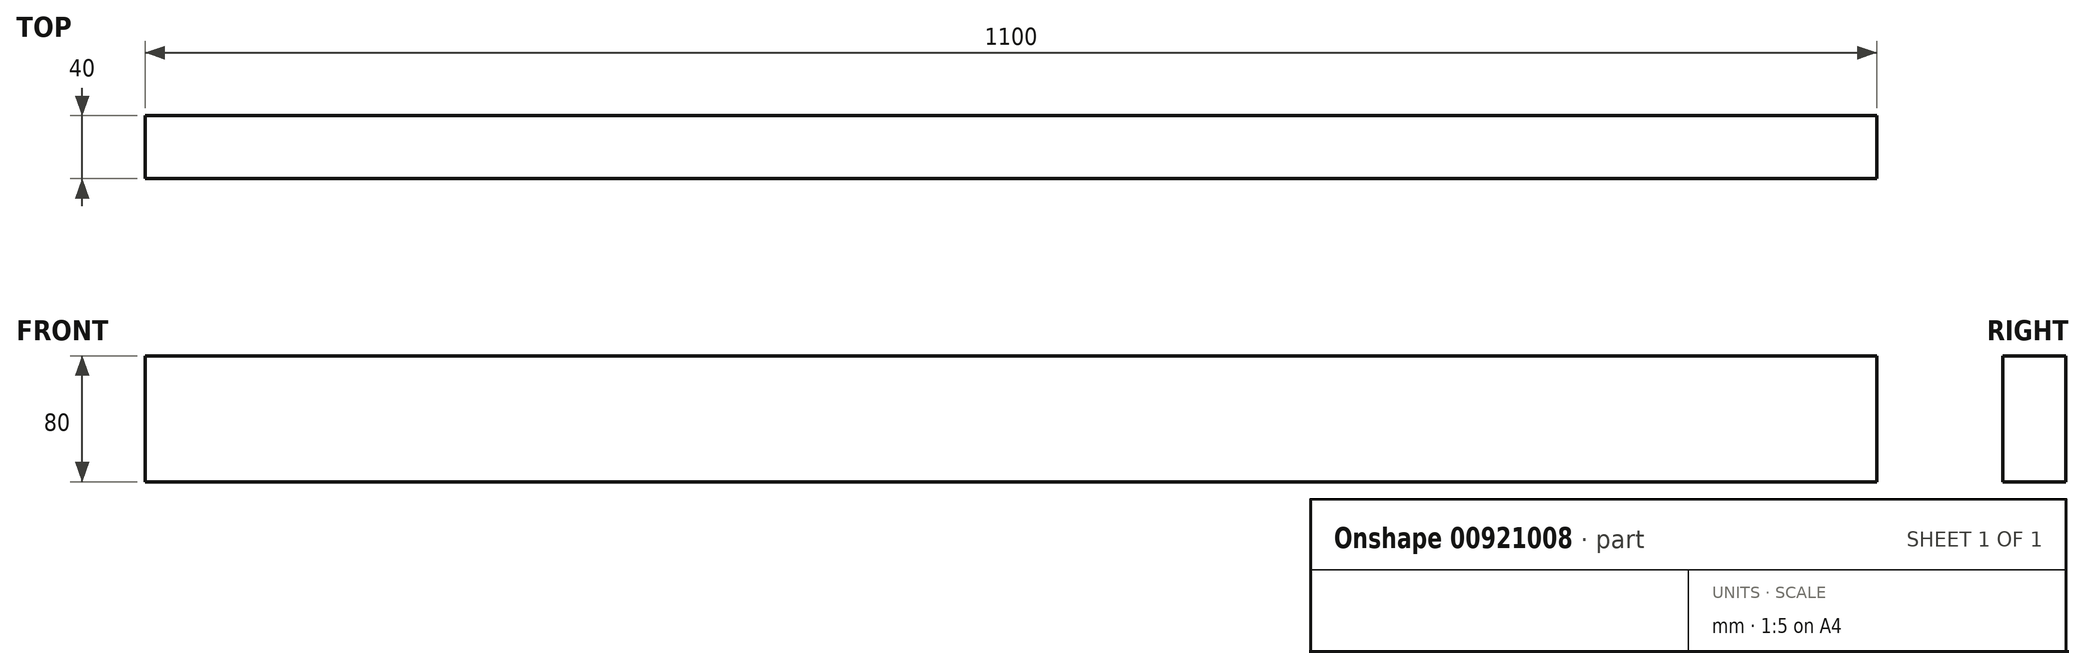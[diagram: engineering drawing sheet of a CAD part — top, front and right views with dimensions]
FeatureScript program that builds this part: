
annotation { "Feature Type Name" : "Feature", "Feature Type Description" : "" }
export const myFeature = defineFeature(function(context is Context, id is Id, definition is map)
    precondition{}
    {
        {
            var Q0;
            Q0=qCreatedBy(makeId("Top.planeOp"),FACE);
            var sketch = newSketch(context, id + "F0", { "sketchPlane" : qUnion([Q0])});
            skLineSegment(sketch, "E0.bottom", {"start": v(-550, 40) * mm, "end": v(550, 40) * mm});
            skLineSegment(sketch, "E0.top", {"start": v(-550, -40) * mm, "end": v(550, -40) * mm});
            skLineSegment(sketch, "E0.left", {"start": v(-550, 40) * mm, "end": v(-550, -40) * mm});
            skLineSegment(sketch, "E0.right", {"start": v(550, 40) * mm, "end": v(550, -40) * mm});
            skPoint(sketch, "E0.middle", {"position": v(0, 0) * mm});
            skSolve(sketch);
        }
        {
            var Q0;
            Q0=makeQuery(id+"F0.imprint","IMPRINT",FACE,{"disambiguationData":[TD([[makeQuery(id+"F0.imprint","IMPRINT",EDGE,{"derivedFrom":sQuery(id+"F0.wireOp",EDGE,"E0.bottom")}),-1.0]])]});
            extrude(context, id + "F1", {"entities" : qUnion([Q0]), "endBound" : BoundingType.SYMMETRIC, "depth" : 40 * mm, "offsetDistance" : 25 * mm});
        }
        {
            var Q0;
            Q0=makeQuery(id+"F1.opExtrude","SWEPT_BODY",BODY,{"disambiguationData":[OSD([sQuery(id+"F0.wireOp",EDGE,"E0.bottom"),sQuery(id+"F0.wireOp",EDGE,"E0.top"),sQuery(id+"F0.wireOp",EDGE,"E0.left"),sQuery(id+"F0.wireOp",EDGE,"E0.right")])]});
            var Q1;
            Q1=makeQuery(id+"F1.opExtrude","CAP_EDGE",EDGE,{"disambiguationData":[OSD([sQuery(id+"F0.wireOp",EDGE,"E0.top")])],"isStart":true});
            transform(context, id + "F2", {"entities" : qUnion([Q0]), "transformType" : TransformType.ROTATION, "transformAxis" : qUnion([Q1]), "angle" : 90 * degree, "makeCopy" : false});
        }
    });
